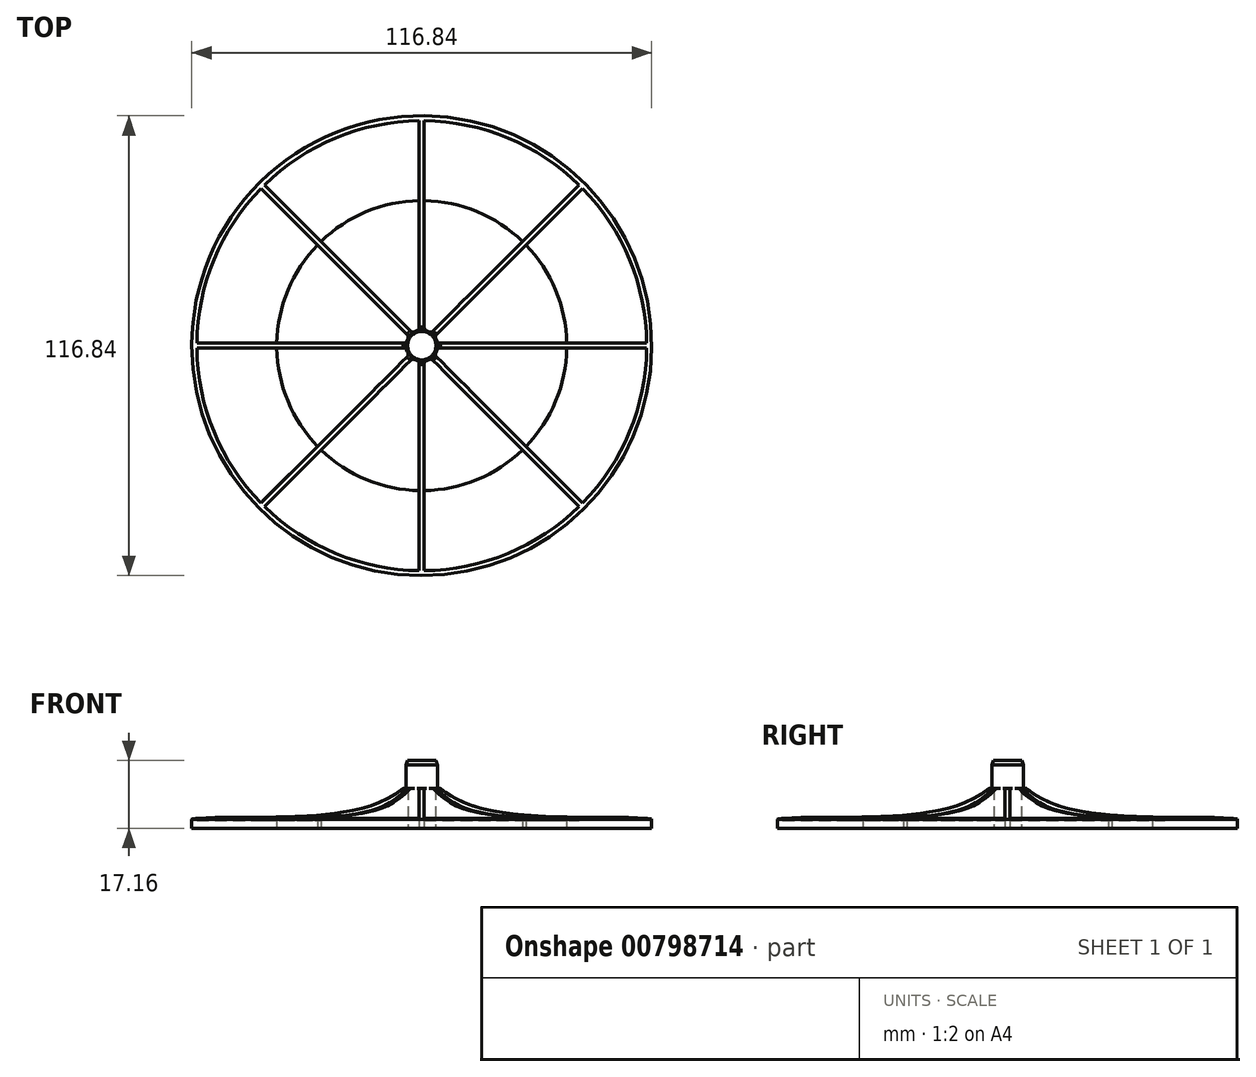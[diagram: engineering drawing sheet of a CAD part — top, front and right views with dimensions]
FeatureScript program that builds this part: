
annotation { "Feature Type Name" : "Feature", "Feature Type Description" : "" }
export const myFeature = defineFeature(function(context is Context, id is Id, definition is map)
    precondition{}
    {
        {
            var Q0;
            Q0=qCreatedBy(makeId("Top.planeOp"),FACE);
            var sketch = newSketch(context, id + "F0", { "sketchPlane" : qUnion([Q0])});
            skCircle(sketch, "E0", {"center": v(0, 0) * mm, "radius": 58.42 * mm});
            skArc(sketch, "E1", {"start": v(-57.15, -0.64) * mm, "mid": v(-52.8, -21.87) * mm, "end": v(-40.86, -39.96) * mm});
            skArc(sketch, "E2", {"start": v(-3.53, 1.87) * mm, "mid": v(-3.7, 1.53) * mm, "end": v(-3.82, 1.17) * mm});
            skLineSegment(sketch, "E3.left", {"start": v(0, 4) * mm, "end": v(0, 3.11) * mm});
            skLineSegment(sketch, "E3.right", {"start": v(0.64, 57.92) * mm, "end": v(0.64, 38.1) * mm});
            skLineSegment(sketch, "E4.MirrorCS", {"start": v(-0.64, 57.92) * mm, "end": v(-0.64, 39.36) * mm});
            skLineSegment(sketch, "E5.1.0", {"start": v(-40.5, 41.4) * mm, "end": v(-26.49, 27.39) * mm});
            skLineSegment(sketch, "E5.1.1", {"start": v(-41.4, 40.5) * mm, "end": v(-27.39, 26.49) * mm});
            skLineSegment(sketch, "E5.2.0", {"start": v(-57.92, 0.64) * mm, "end": v(-38.1, 0.64) * mm});
            skLineSegment(sketch, "E5.2.1", {"start": v(-57.92, -0.64) * mm, "end": v(-39.36, -0.64) * mm});
            skLineSegment(sketch, "E5.3.0", {"start": v(-41.4, -40.5) * mm, "end": v(-27.39, -26.49) * mm});
            skLineSegment(sketch, "E5.3.1", {"start": v(-40.5, -41.4) * mm, "end": v(-27.39, -28.28) * mm});
            skLineSegment(sketch, "E5.4.0", {"start": v(-0.64, -57.92) * mm, "end": v(-0.64, -38.1) * mm});
            skLineSegment(sketch, "E5.4.1", {"start": v(0.64, -57.92) * mm, "end": v(0.64, -39.36) * mm});
            skLineSegment(sketch, "E5.5.0", {"start": v(40.5, -41.4) * mm, "end": v(27.39, -28.28) * mm});
            skLineSegment(sketch, "E5.5.1", {"start": v(41.4, -40.5) * mm, "end": v(27.39, -26.49) * mm});
            skLineSegment(sketch, "E5.6.0", {"start": v(57.92, -0.64) * mm, "end": v(38.1, -0.64) * mm});
            skLineSegment(sketch, "E5.6.1", {"start": v(57.92, 0.63) * mm, "end": v(39.36, 0.63) * mm});
            skLineSegment(sketch, "E5.7.0", {"start": v(41.4, 40.5) * mm, "end": v(28.28, 27.39) * mm});
            skLineSegment(sketch, "E5.7.1", {"start": v(40.5, 41.4) * mm, "end": v(26.49, 27.39) * mm});
            skArc(sketch, "E6.trimOffspring", {"start": v(-39.96, -40.86) * mm, "mid": v(-21.87, -52.8) * mm, "end": v(-0.64, -57.15) * mm});
            skArc(sketch, "E7.trimOffspring", {"start": v(0.63, -57.15) * mm, "mid": v(21.87, -52.8) * mm, "end": v(39.96, -40.86) * mm});
            skArc(sketch, "E8.trimOffspring", {"start": v(40.86, -39.96) * mm, "mid": v(52.8, -21.87) * mm, "end": v(57.15, -0.64) * mm});
            skArc(sketch, "E9.trimOffspring", {"start": v(57.15, 0.63) * mm, "mid": v(52.8, 21.87) * mm, "end": v(40.86, 39.96) * mm});
            skArc(sketch, "E10.trimOffspring", {"start": v(39.96, 40.86) * mm, "mid": v(21.87, 52.8) * mm, "end": v(0.64, 57.15) * mm});
            skArc(sketch, "E11.trimOffspring", {"start": v(-0.64, 57.15) * mm, "mid": v(-21.87, 52.8) * mm, "end": v(-39.96, 40.86) * mm});
            skPoint(sketch, "E12.orphan", {"position": v(0, 57.15) * mm});
            skArc(sketch, "E13.trimOffspring", {"start": v(-40.86, 39.96) * mm, "mid": v(-52.8, 21.87) * mm, "end": v(-57.15, 0.64) * mm});
            skArc(sketch, "E14.trimOffspring", {"start": v(-3.82, -1.17) * mm, "mid": v(-3.7, -1.53) * mm, "end": v(-3.53, -1.87) * mm});
            skArc(sketch, "E15.trimOffspring", {"start": v(-1.87, -3.53) * mm, "mid": v(-1.53, -3.7) * mm, "end": v(-1.17, -3.82) * mm});
            skArc(sketch, "E16.trimOffspring", {"start": v(1.17, -3.82) * mm, "mid": v(1.53, -3.7) * mm, "end": v(1.87, -3.53) * mm});
            skArc(sketch, "E17.trimOffspring", {"start": v(3.53, -1.87) * mm, "mid": v(3.7, -1.53) * mm, "end": v(3.82, -1.17) * mm});
            skArc(sketch, "E18.trimOffspring", {"start": v(3.82, 1.17) * mm, "mid": v(3.7, 1.53) * mm, "end": v(3.53, 1.87) * mm});
            skArc(sketch, "E19.trimOffspring", {"start": v(1.87, 3.53) * mm, "mid": v(1.53, 3.7) * mm, "end": v(1.17, 3.82) * mm});
            skArc(sketch, "E20.trimOffspring", {"start": v(-1.17, 3.82) * mm, "mid": v(-1.53, 3.7) * mm, "end": v(-1.87, 3.53) * mm});
            skPoint(sketch, "E21.visualSharp", {"position": v(-3.24, 2.34) * mm});
            skArc(sketch, "E21.filletArc", {"start": v(-3.53, 1.87) * mm, "mid": v(-3.45, 2.34) * mm, "end": v(-3.67, 2.77) * mm});
            skPoint(sketch, "E22.visualSharp", {"position": v(-3.95, 0.63) * mm});
            skArc(sketch, "E22.filletArc", {"start": v(-4.55, 0.64) * mm, "mid": v(-4.1, 0.78) * mm, "end": v(-3.82, 1.17) * mm});
            skPoint(sketch, "E23.visualSharp", {"position": v(-3.95, -0.64) * mm});
            skArc(sketch, "E23.filletArc", {"start": v(-3.82, -1.17) * mm, "mid": v(-4.1, -0.78) * mm, "end": v(-4.55, -0.64) * mm});
            skPoint(sketch, "E24.visualSharp", {"position": v(-3.24, -2.34) * mm});
            skArc(sketch, "E24.filletArc", {"start": v(-3.67, -2.77) * mm, "mid": v(-3.45, -2.34) * mm, "end": v(-3.53, -1.87) * mm});
            skPoint(sketch, "E25.visualSharp", {"position": v(-2.34, -3.24) * mm});
            skArc(sketch, "E25.filletArc", {"start": v(-1.87, -3.53) * mm, "mid": v(-2.34, -3.45) * mm, "end": v(-2.77, -3.67) * mm});
            skPoint(sketch, "E26.visualSharp", {"position": v(-0.63, -3.95) * mm});
            skArc(sketch, "E26.filletArc", {"start": v(-0.64, -4.55) * mm, "mid": v(-0.78, -4.1) * mm, "end": v(-1.17, -3.82) * mm});
            skPoint(sketch, "E27.visualSharp", {"position": v(0.63, -3.95) * mm});
            skArc(sketch, "E27.filletArc", {"start": v(1.17, -3.82) * mm, "mid": v(0.78, -4.1) * mm, "end": v(0.63, -4.55) * mm});
            skPoint(sketch, "E28.visualSharp", {"position": v(2.34, -3.24) * mm});
            skArc(sketch, "E28.filletArc", {"start": v(2.77, -3.67) * mm, "mid": v(2.34, -3.45) * mm, "end": v(1.87, -3.53) * mm});
            skPoint(sketch, "E29.visualSharp", {"position": v(3.24, -2.34) * mm});
            skArc(sketch, "E29.filletArc", {"start": v(3.53, -1.87) * mm, "mid": v(3.45, -2.34) * mm, "end": v(3.67, -2.77) * mm});
            skPoint(sketch, "E30.visualSharp", {"position": v(3.95, -0.63) * mm});
            skArc(sketch, "E30.filletArc", {"start": v(4.55, -0.64) * mm, "mid": v(4.1, -0.78) * mm, "end": v(3.82, -1.17) * mm});
            skPoint(sketch, "E31.visualSharp", {"position": v(3.95, 0.63) * mm});
            skArc(sketch, "E31.filletArc", {"start": v(3.82, 1.17) * mm, "mid": v(4.1, 0.78) * mm, "end": v(4.55, 0.63) * mm});
            skPoint(sketch, "E32.visualSharp", {"position": v(3.24, 2.34) * mm});
            skArc(sketch, "E32.filletArc", {"start": v(3.67, 2.77) * mm, "mid": v(3.45, 2.34) * mm, "end": v(3.53, 1.87) * mm});
            skPoint(sketch, "E33.visualSharp", {"position": v(2.34, 3.24) * mm});
            skArc(sketch, "E33.filletArc", {"start": v(1.87, 3.53) * mm, "mid": v(2.34, 3.45) * mm, "end": v(2.77, 3.67) * mm});
            skPoint(sketch, "E34.visualSharp", {"position": v(0.63, 3.95) * mm});
            skArc(sketch, "E34.filletArc", {"start": v(0.64, 4.55) * mm, "mid": v(0.78, 4.1) * mm, "end": v(1.17, 3.82) * mm});
            skPoint(sketch, "E35.visualSharp", {"position": v(-0.63, 3.95) * mm});
            skArc(sketch, "E35.filletArc", {"start": v(-1.17, 3.82) * mm, "mid": v(-0.78, 4.1) * mm, "end": v(-0.63, 4.55) * mm});
            skPoint(sketch, "E36.visualSharp", {"position": v(-2.34, 3.24) * mm});
            skArc(sketch, "E36.filletArc", {"start": v(-2.77, 3.67) * mm, "mid": v(-2.34, 3.45) * mm, "end": v(-1.87, 3.53) * mm});
            skLineSegment(sketch, "E37.trimOffspring", {"start": v(26.49, 27.39) * mm, "end": v(2.77, 3.67) * mm});
            skLineSegment(sketch, "E38.trimOffspring", {"start": v(28.28, 27.39) * mm, "end": v(3.67, 2.77) * mm});
            skLineSegment(sketch, "E39.trimOffspring", {"start": v(39.36, 0.63) * mm, "end": v(4.55, 0.63) * mm});
            skLineSegment(sketch, "E40.trimOffspring", {"start": v(38.1, -0.64) * mm, "end": v(4.55, -0.64) * mm});
            skLineSegment(sketch, "E41.trimOffspring", {"start": v(-26.49, 27.39) * mm, "end": v(-2.77, 3.67) * mm});
            skLineSegment(sketch, "E42.trimOffspring", {"start": v(-27.39, 26.49) * mm, "end": v(-3.67, 2.77) * mm});
            skLineSegment(sketch, "E43.trimOffspring", {"start": v(-0.64, 39.36) * mm, "end": v(-0.64, 4.55) * mm});
            skLineSegment(sketch, "E44.trimOffspring", {"start": v(0.64, 38.1) * mm, "end": v(0.64, 4.55) * mm});
            skLineSegment(sketch, "E45.trimOffspring", {"start": v(-39.36, -0.64) * mm, "end": v(-4.55, -0.64) * mm});
            skLineSegment(sketch, "E46.trimOffspring", {"start": v(-38.1, 0.64) * mm, "end": v(-4.55, 0.64) * mm});
            skLineSegment(sketch, "E47.trimOffspring", {"start": v(-27.39, -26.49) * mm, "end": v(-3.67, -2.77) * mm});
            skLineSegment(sketch, "E48.trimOffspring", {"start": v(-27.39, -28.28) * mm, "end": v(-2.77, -3.67) * mm});
            skLineSegment(sketch, "E49.trimOffspring", {"start": v(-0.64, -38.1) * mm, "end": v(-0.64, -4.55) * mm});
            skLineSegment(sketch, "E50.trimOffspring", {"start": v(0.64, -39.36) * mm, "end": v(0.63, -4.55) * mm});
            skLineSegment(sketch, "E51.trimOffspring", {"start": v(27.39, -26.49) * mm, "end": v(3.67, -2.77) * mm});
            skLineSegment(sketch, "E52.trimOffspring", {"start": v(27.39, -28.28) * mm, "end": v(2.77, -3.67) * mm});
            skSolve(sketch);
        }
        {
            var Q0;
            Q0=makeQuery(id+"F0.imprint","IMPRINT",FACE,{"disambiguationData":[TD([[makeQuery(id+"F0.imprint","IMPRINT",EDGE,{"derivedFrom":sQuery(id+"F0.wireOp",EDGE,"E0")}),1.0]])]});
            extrude(context, id + "F1", {"entities" : qUnion([Q0]), "depth" : 10.16 * mm, "offsetDistance" : 25.4 * mm});
        }
        {
            var Q0;
            Q0=qCreatedBy(makeId("Top.planeOp"),FACE);
            var sketch = newSketch(context, id + "F2", { "sketchPlane" : qUnion([Q0])});
            skCircle(sketch, "E53", {"center": v(0, 0) * mm, "radius": 58.42 * mm});
            skCircle(sketch, "E54", {"center": v(0, 0) * mm, "radius": 36.83 * mm});
            skSolve(sketch);
        }
        {
            var Q0;
            Q0=qSketchRegion(id+"F2",true);
            extrude(context, id + "F3", {"entities" : qUnion([Q0]), "operationType" : NewBodyOperationType.ADD, "depth" : 2 * mm, "offsetDistance" : 25.4 * mm});
        }
        {
            var Q0;
            Q0=qCreatedBy(makeId("Right.planeOp"),FACE);
            var sketch = newSketch(context, id + "F4", { "sketchPlane" : qUnion([Q0])});
            skLineSegment(sketch, "E55.bottom", {"start": v(0, 24.07) * mm, "end": v(62.34, 24.07) * mm});
            skLineSegment(sketch, "E55.left", {"start": v(0, 24.07) * mm, "end": v(0, 16.63) * mm});
            skLineSegment(sketch, "E55.right", {"start": v(62.34, 24.07) * mm, "end": v(62.34, 0) * mm});
            skPoint(sketch, "E55.top.start.orphan", {"position": v(0, 9.19) * mm});
            skFitSpline(sketch, "E56", {"points": [v(0, 16.63) * mm, v(12.4, 5.88) * mm, v(52.5, 2.67) * mm, v(62.34, 0) * mm], "startDerivative": vector(15.3, -40.46) * mm, "endDerivative": vector(6.57, -27.93) * mm});
            skLineSegment(sketch, "E57.top", {"start": v(36.88, 0) * mm, "end": v(38.1, 0) * mm});
            skLineSegment(sketch, "E58", {"start": v(0, 0) * mm, "end": v(38.1, 0) * mm});
            skSolve(sketch);
        }
        {
            var Q0;
            Q0=makeQuery(id+"F4.imprint","IMPRINT",FACE,{"disambiguationData":[TD([[makeQuery(id+"F4.imprint","IMPRINT",EDGE,{"derivedFrom":sQuery(id+"F4.wireOp",EDGE,"E57.bottom")}),-1.0]])]});
            var Q1;
            Q1=makeQuery(id+"F4.imprint","IMPRINT",FACE,{"disambiguationData":[TD([[makeQuery(id+"F4.imprint","IMPRINT",EDGE,{"derivedFrom":sQuery(id+"F4.wireOp",EDGE,"E55.bottom")}),-1.0]])]});
            var Q2;
            Q2=makeQuery(id+"F1.opExtrude","SWEPT_FACE",FACE,{"disambiguationData":[OSD([sQuery(id+"F0.wireOp",EDGE,"E0")])]});
            revolve(context, id + "F5", {"operationType" : NewBodyOperationType.REMOVE, "surfaceOperationType" : NewSurfaceOperationType.NEW, "entities" : qUnion([Q0, Q1]), "axis" : qUnion([Q2]), "revolveType" : RevolveType.FULL, "oppositeDirection" : true});
        }
        {
            var Q0;
            Q0=makeQuery(id+"F1.opExtrude","CAP_FACE",FACE,{"disambiguationData":[OSD([sQuery(id+"F0.wireOp",EDGE,"E0"),sQuery(id+"F0.wireOp",EDGE,"E1"),sQuery(id+"F0.wireOp",EDGE,"E2"),sQuery(id+"F0.wireOp",EDGE,"E3.right"),sQuery(id+"F0.wireOp",EDGE,"E4.MirrorCS"),sQuery(id+"F0.wireOp",EDGE,"E5.1.0"),sQuery(id+"F0.wireOp",EDGE,"E5.1.1"),sQuery(id+"F0.wireOp",EDGE,"E5.2.0"),sQuery(id+"F0.wireOp",EDGE,"E5.2.1"),sQuery(id+"F0.wireOp",EDGE,"E5.3.0"),sQuery(id+"F0.wireOp",EDGE,"E5.3.1"),sQuery(id+"F0.wireOp",EDGE,"E5.4.0"),sQuery(id+"F0.wireOp",EDGE,"E5.4.1"),sQuery(id+"F0.wireOp",EDGE,"E5.5.0"),sQuery(id+"F0.wireOp",EDGE,"E5.5.1"),sQuery(id+"F0.wireOp",EDGE,"E5.6.0"),sQuery(id+"F0.wireOp",EDGE,"E5.6.1"),sQuery(id+"F0.wireOp",EDGE,"E5.7.0"),sQuery(id+"F0.wireOp",EDGE,"E5.7.1"),sQuery(id+"F0.wireOp",EDGE,"E6.trimOffspring"),sQuery(id+"F0.wireOp",EDGE,"E7.trimOffspring"),sQuery(id+"F0.wireOp",EDGE,"E8.trimOffspring"),sQuery(id+"F0.wireOp",EDGE,"E9.trimOffspring"),sQuery(id+"F0.wireOp",EDGE,"E10.trimOffspring"),sQuery(id+"F0.wireOp",EDGE,"E11.trimOffspring"),sQuery(id+"F0.wireOp",EDGE,"E13.trimOffspring"),sQuery(id+"F0.wireOp",EDGE,"E14.trimOffspring"),sQuery(id+"F0.wireOp",EDGE,"E15.trimOffspring"),sQuery(id+"F0.wireOp",EDGE,"E16.trimOffspring"),sQuery(id+"F0.wireOp",EDGE,"E17.trimOffspring"),sQuery(id+"F0.wireOp",EDGE,"E18.trimOffspring"),sQuery(id+"F0.wireOp",EDGE,"E19.trimOffspring"),sQuery(id+"F0.wireOp",EDGE,"E20.trimOffspring"),sQuery(id+"F0.wireOp",EDGE,"E21.filletArc"),sQuery(id+"F0.wireOp",EDGE,"E22.filletArc"),sQuery(id+"F0.wireOp",EDGE,"E23.filletArc"),sQuery(id+"F0.wireOp",EDGE,"E24.filletArc"),sQuery(id+"F0.wireOp",EDGE,"E25.filletArc"),sQuery(id+"F0.wireOp",EDGE,"E26.filletArc"),sQuery(id+"F0.wireOp",EDGE,"E27.filletArc"),sQuery(id+"F0.wireOp",EDGE,"E28.filletArc"),sQuery(id+"F0.wireOp",EDGE,"E29.filletArc"),sQuery(id+"F0.wireOp",EDGE,"E30.filletArc"),sQuery(id+"F0.wireOp",EDGE,"E31.filletArc"),sQuery(id+"F0.wireOp",EDGE,"E32.filletArc"),sQuery(id+"F0.wireOp",EDGE,"E33.filletArc"),sQuery(id+"F0.wireOp",EDGE,"E34.filletArc"),sQuery(id+"F0.wireOp",EDGE,"E35.filletArc"),sQuery(id+"F0.wireOp",EDGE,"E36.filletArc"),sQuery(id+"F0.wireOp",EDGE,"E37.trimOffspring"),sQuery(id+"F0.wireOp",EDGE,"E38.trimOffspring"),sQuery(id+"F0.wireOp",EDGE,"E39.trimOffspring"),sQuery(id+"F0.wireOp",EDGE,"E40.trimOffspring"),sQuery(id+"F0.wireOp",EDGE,"E41.trimOffspring"),sQuery(id+"F0.wireOp",EDGE,"E42.trimOffspring"),sQuery(id+"F0.wireOp",EDGE,"E43.trimOffspring"),sQuery(id+"F0.wireOp",EDGE,"E44.trimOffspring"),sQuery(id+"F0.wireOp",EDGE,"E45.trimOffspring"),sQuery(id+"F0.wireOp",EDGE,"E46.trimOffspring"),sQuery(id+"F0.wireOp",EDGE,"E47.trimOffspring"),sQuery(id+"F0.wireOp",EDGE,"E48.trimOffspring"),sQuery(id+"F0.wireOp",EDGE,"E49.trimOffspring"),sQuery(id+"F0.wireOp",EDGE,"E50.trimOffspring"),sQuery(id+"F0.wireOp",EDGE,"E51.trimOffspring"),sQuery(id+"F0.wireOp",EDGE,"E52.trimOffspring")])],"isStart":false});
            var sketch = newSketch(context, id + "F6", { "sketchPlane" : qUnion([Q0])});
            skCircle(sketch, "E59", {"center": v(0, 0) * mm, "radius": 4 * mm});
            skSolve(sketch);
        }
        {
            var Q0;
            {var subQ0=sQuery(id+"F6.wireOp",EDGE,"E59");var subQ4=makeQuery(id+"F6.imprint","INTERSECT",VERTEX,{"derivedFrom":[makeQuery(id+"F1.opExtrude","CAP_EDGE",EDGE,{"disambiguationData":[OSD([sQuery(id+"F0.wireOp",EDGE,"E33.filletArc")])],"isStart":false}),subQ0]});Q0=makeQuery(id+"F6.imprint","IMPRINT",FACE,{"disambiguationData":[TD([[makeQuery(id+"F6.imprint","IMPRINT",EDGE,{"disambiguationData":[TD([[subQ4,-1.0]])],"derivedFrom":subQ0}),1.0]])]});}
            extrude(context, id + "F7", {"entities" : qUnion([Q0]), "operationType" : NewBodyOperationType.ADD, "depth" : 7 * mm, "offsetDistance" : 25.4 * mm});
        }
        {
            var Q0;
            Q0=makeQuery(id+"F7.opExtrude","CAP_EDGE",EDGE,{"disambiguationData":[OSD([sQuery(id+"F6.wireOp",EDGE,"E59")])],"isStart":false});
            chamfer(context, id + "F8", {"entities" : qUnion([Q0]), "chamferType" : ChamferType.OFFSET_ANGLE, "width" : 0.38 * mm, "oppositeDirection" : false, "angle" : 70 * degree, "tangentPropagation" : true});
        }
    });
